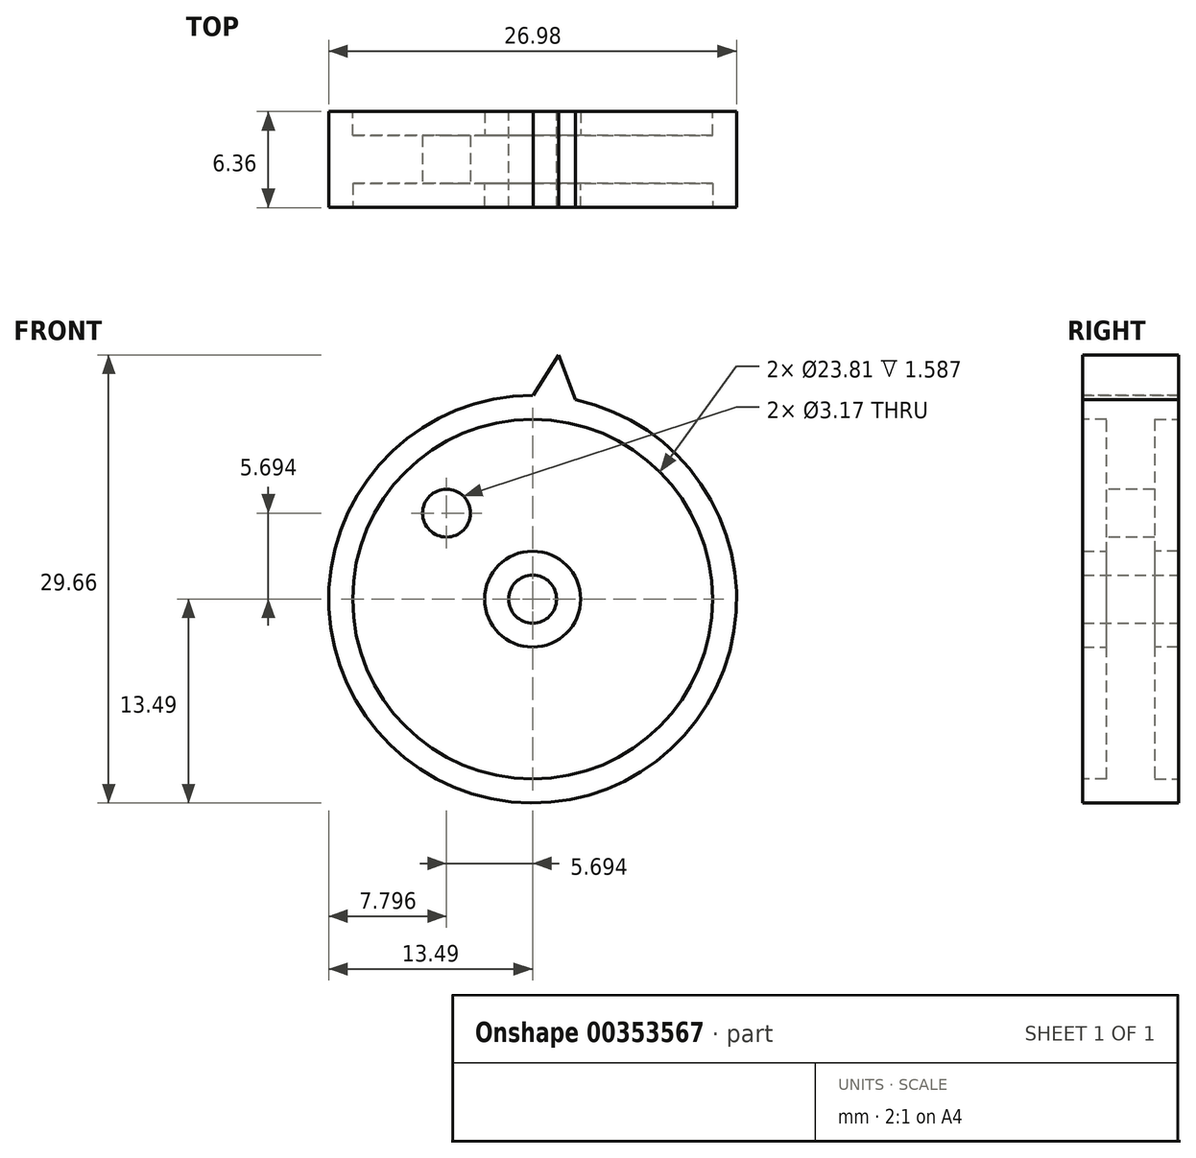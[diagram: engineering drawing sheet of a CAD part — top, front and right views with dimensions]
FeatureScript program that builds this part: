
annotation { "Feature Type Name" : "Feature", "Feature Type Description" : "" }
export const myFeature = defineFeature(function(context is Context, id is Id, definition is map)
    precondition{}
    {
        {
            var Q0;
            Q0=qCreatedBy(makeId("Front.planeOp"),FACE);
            var sketch = newSketch(context, id + "F0", { "sketchPlane" : qUnion([Q0])});
            skCircle(sketch, "E0", {"center": v(0, 0) * mm, "radius": 13.5 * mm});
            skSolve(sketch);
        }
        {
            var Q0;
            Q0 = qSketchRegion(id + "F0", true);
            extrude(context, id + "F1", {"entities" : qUnion([Q0]), "depth" : 6.35 * mm, "symmetric" : true});
        }
        {
            var Q0;
            Q0=makeQuery(id+"F1.opExtrude","CAP_FACE",FACE,{"disambiguationData":[OSD([sQuery(id+"F0.wireOp",EDGE,"E0")])],"isStart":false});
            var sketch = newSketch(context, id + "F2", { "sketchPlane" : qUnion([Q0])});
            skLineSegment(sketch, "E1", {"start": v(0.02, 13.5) * mm, "end": v(1.73, 16.17) * mm});
            skLineSegment(sketch, "E2", {"start": v(1.73, 16.17) * mm, "end": v(2.83, 13.2) * mm});
            skLineSegment(sketch, "E3", {"start": v(0, 0) * mm, "end": v(0.02, 13.5) * mm, "construction": true});
            skLineSegment(sketch, "E4", {"start": v(0, 0) * mm, "end": v(2.83, 13.2) * mm, "construction": true});
            skArc(sketch, "E5.0", {"start": v(2.83, 13.2) * mm, "mid": v(1.43, 13.42) * mm, "end": v(0.02, 13.5) * mm});
            skSolve(sketch);
        }
        {
            var Q0;
            Q0 = qSketchRegion(id + "F2", true);
            extrude(context, id + "F3", {"entities" : qUnion([Q0]), "operationType" : NewBodyOperationType.ADD, "oppositeDirection" : true, "depth" : 6.35 * mm});
        }
        {
            var Q0;
            {var subQ0=sQuery(id+"F2.wireOp",EDGE,"E5.0");var subQ1=sQuery(id+"F2.wireOp",EDGE,"E2");var subQ2=sQuery(id+"F2.wireOp",EDGE,"E1");Q0=makeQuery(id+"Fj7QE7v1GZ9bRCr_1.29.F3.boolean.opBoolean","MERGE",FACE,{"derivedFrom":[makeQuery(id+"Fj7QE7v1GZ9bRCr_1.28.F3.boolean.opBoolean","MERGE",FACE,{"derivedFrom":[makeQuery(id+"Fj7QE7v1GZ9bRCr_1.27.F3.boolean.opBoolean","MERGE",FACE,{"derivedFrom":[makeQuery(id+"Fj7QE7v1GZ9bRCr_1.26.F3.boolean.opBoolean","MERGE",FACE,{"derivedFrom":[makeQuery(id+"Fj7QE7v1GZ9bRCr_1.25.F3.boolean.opBoolean","MERGE",FACE,{"derivedFrom":[makeQuery(id+"Fj7QE7v1GZ9bRCr_1.24.F3.boolean.opBoolean","MERGE",FACE,{"derivedFrom":[makeQuery(id+"Fj7QE7v1GZ9bRCr_1.23.F3.boolean.opBoolean","MERGE",FACE,{"derivedFrom":[makeQuery(id+"Fj7QE7v1GZ9bRCr_1.22.F3.boolean.opBoolean","MERGE",FACE,{"derivedFrom":[makeQuery(id+"Fj7QE7v1GZ9bRCr_1.21.F3.boolean.opBoolean","MERGE",FACE,{"derivedFrom":[makeQuery(id+"Fj7QE7v1GZ9bRCr_1.20.F3.boolean.opBoolean","MERGE",FACE,{"derivedFrom":[makeQuery(id+"Fj7QE7v1GZ9bRCr_1.19.F3.boolean.opBoolean","MERGE",FACE,{"derivedFrom":[makeQuery(id+"Fj7QE7v1GZ9bRCr_1.18.F3.boolean.opBoolean","MERGE",FACE,{"derivedFrom":[makeQuery(id+"Fj7QE7v1GZ9bRCr_1.17.F3.boolean.opBoolean","MERGE",FACE,{"derivedFrom":[makeQuery(id+"Fj7QE7v1GZ9bRCr_1.16.F3.boolean.opBoolean","MERGE",FACE,{"derivedFrom":[makeQuery(id+"Fj7QE7v1GZ9bRCr_1.15.F3.boolean.opBoolean","MERGE",FACE,{"derivedFrom":[makeQuery(id+"Fj7QE7v1GZ9bRCr_1.14.F3.boolean.opBoolean","MERGE",FACE,{"derivedFrom":[makeQuery(id+"Fj7QE7v1GZ9bRCr_1.13.F3.boolean.opBoolean","MERGE",FACE,{"derivedFrom":[makeQuery(id+"Fj7QE7v1GZ9bRCr_1.12.F3.boolean.opBoolean","MERGE",FACE,{"derivedFrom":[makeQuery(id+"Fj7QE7v1GZ9bRCr_1.11.F3.boolean.opBoolean","MERGE",FACE,{"derivedFrom":[makeQuery(id+"Fj7QE7v1GZ9bRCr_1.10.F3.boolean.opBoolean","MERGE",FACE,{"derivedFrom":[makeQuery(id+"Fj7QE7v1GZ9bRCr_1.9.F3.boolean.opBoolean","MERGE",FACE,{"derivedFrom":[makeQuery(id+"Fj7QE7v1GZ9bRCr_1.8.F3.boolean.opBoolean","MERGE",FACE,{"derivedFrom":[makeQuery(id+"Fj7QE7v1GZ9bRCr_1.7.F3.boolean.opBoolean","MERGE",FACE,{"derivedFrom":[makeQuery(id+"Fj7QE7v1GZ9bRCr_1.6.F3.boolean.opBoolean","MERGE",FACE,{"derivedFrom":[makeQuery(id+"Fj7QE7v1GZ9bRCr_1.5.F3.boolean.opBoolean","MERGE",FACE,{"derivedFrom":[makeQuery(id+"Fj7QE7v1GZ9bRCr_1.4.F3.boolean.opBoolean","MERGE",FACE,{"derivedFrom":[makeQuery(id+"Fj7QE7v1GZ9bRCr_1.3.F3.boolean.opBoolean","MERGE",FACE,{"derivedFrom":[makeQuery(id+"Fj7QE7v1GZ9bRCr_1.2.F3.boolean.opBoolean","MERGE",FACE,{"derivedFrom":[makeQuery(id+"Fj7QE7v1GZ9bRCr_1.1.F3.boolean.opBoolean","MERGE",FACE,{"derivedFrom":[makeQuery(id+"F3.boolean.opBoolean","MERGE",FACE,{"derivedFrom":[makeQuery(id+"F1.opExtrude","CAP_FACE",FACE,{"disambiguationData":[OSD([sQuery(id+"F0.wireOp",EDGE,"E0")])],"isStart":false}),makeQuery(id+"F3.opExtrude","CAP_FACE",FACE,{"disambiguationData":[OSD([subQ2,subQ1,subQ0])],"isStart":true})]}),makeQuery(id+"Fj7QE7v1GZ9bRCr_1.1.F3.opExtrude","CAP_FACE",FACE,{"disambiguationData":[OSD([subQ2,subQ1,subQ0])],"isStart":true})]}),makeQuery(id+"Fj7QE7v1GZ9bRCr_1.2.F3.opExtrude","CAP_FACE",FACE,{"disambiguationData":[OSD([subQ2,subQ1,subQ0])],"isStart":true})]}),makeQuery(id+"Fj7QE7v1GZ9bRCr_1.3.F3.opExtrude","CAP_FACE",FACE,{"disambiguationData":[OSD([subQ2,subQ1,subQ0])],"isStart":true})]}),makeQuery(id+"Fj7QE7v1GZ9bRCr_1.4.F3.opExtrude","CAP_FACE",FACE,{"disambiguationData":[OSD([subQ2,subQ1,subQ0])],"isStart":true})]}),makeQuery(id+"Fj7QE7v1GZ9bRCr_1.5.F3.opExtrude","CAP_FACE",FACE,{"disambiguationData":[OSD([subQ2,subQ1,subQ0])],"isStart":true})]}),makeQuery(id+"Fj7QE7v1GZ9bRCr_1.6.F3.opExtrude","CAP_FACE",FACE,{"disambiguationData":[OSD([subQ2,subQ1,subQ0])],"isStart":true})]}),makeQuery(id+"Fj7QE7v1GZ9bRCr_1.7.F3.opExtrude","CAP_FACE",FACE,{"disambiguationData":[OSD([subQ2,subQ1,subQ0])],"isStart":true})]}),makeQuery(id+"Fj7QE7v1GZ9bRCr_1.8.F3.opExtrude","CAP_FACE",FACE,{"disambiguationData":[OSD([subQ2,subQ1,subQ0])],"isStart":true})]}),makeQuery(id+"Fj7QE7v1GZ9bRCr_1.9.F3.opExtrude","CAP_FACE",FACE,{"disambiguationData":[OSD([subQ2,subQ1,subQ0])],"isStart":true})]}),makeQuery(id+"Fj7QE7v1GZ9bRCr_1.10.F3.opExtrude","CAP_FACE",FACE,{"disambiguationData":[OSD([subQ2,subQ1,subQ0])],"isStart":true})]}),makeQuery(id+"Fj7QE7v1GZ9bRCr_1.11.F3.opExtrude","CAP_FACE",FACE,{"disambiguationData":[OSD([subQ2,subQ1,subQ0])],"isStart":true})]}),makeQuery(id+"Fj7QE7v1GZ9bRCr_1.12.F3.opExtrude","CAP_FACE",FACE,{"disambiguationData":[OSD([subQ2,subQ1,subQ0])],"isStart":true})]}),makeQuery(id+"Fj7QE7v1GZ9bRCr_1.13.F3.opExtrude","CAP_FACE",FACE,{"disambiguationData":[OSD([subQ2,subQ1,subQ0])],"isStart":true})]}),makeQuery(id+"Fj7QE7v1GZ9bRCr_1.14.F3.opExtrude","CAP_FACE",FACE,{"disambiguationData":[OSD([subQ2,subQ1,subQ0])],"isStart":true})]}),makeQuery(id+"Fj7QE7v1GZ9bRCr_1.15.F3.opExtrude","CAP_FACE",FACE,{"disambiguationData":[OSD([subQ2,subQ1,subQ0])],"isStart":true})]}),makeQuery(id+"Fj7QE7v1GZ9bRCr_1.16.F3.opExtrude","CAP_FACE",FACE,{"disambiguationData":[OSD([subQ2,subQ1,subQ0])],"isStart":true})]}),makeQuery(id+"Fj7QE7v1GZ9bRCr_1.17.F3.opExtrude","CAP_FACE",FACE,{"disambiguationData":[OSD([subQ2,subQ1,subQ0])],"isStart":true})]}),makeQuery(id+"Fj7QE7v1GZ9bRCr_1.18.F3.opExtrude","CAP_FACE",FACE,{"disambiguationData":[OSD([subQ2,subQ1,subQ0])],"isStart":true})]}),makeQuery(id+"Fj7QE7v1GZ9bRCr_1.19.F3.opExtrude","CAP_FACE",FACE,{"disambiguationData":[OSD([subQ2,subQ1,subQ0])],"isStart":true})]}),makeQuery(id+"Fj7QE7v1GZ9bRCr_1.20.F3.opExtrude","CAP_FACE",FACE,{"disambiguationData":[OSD([subQ2,subQ1,subQ0])],"isStart":true})]}),makeQuery(id+"Fj7QE7v1GZ9bRCr_1.21.F3.opExtrude","CAP_FACE",FACE,{"disambiguationData":[OSD([subQ2,subQ1,subQ0])],"isStart":true})]}),makeQuery(id+"Fj7QE7v1GZ9bRCr_1.22.F3.opExtrude","CAP_FACE",FACE,{"disambiguationData":[OSD([subQ2,subQ1,subQ0])],"isStart":true})]}),makeQuery(id+"Fj7QE7v1GZ9bRCr_1.23.F3.opExtrude","CAP_FACE",FACE,{"disambiguationData":[OSD([subQ2,subQ1,subQ0])],"isStart":true})]}),makeQuery(id+"Fj7QE7v1GZ9bRCr_1.24.F3.opExtrude","CAP_FACE",FACE,{"disambiguationData":[OSD([subQ2,subQ1,subQ0])],"isStart":true})]}),makeQuery(id+"Fj7QE7v1GZ9bRCr_1.25.F3.opExtrude","CAP_FACE",FACE,{"disambiguationData":[OSD([subQ2,subQ1,subQ0])],"isStart":true})]}),makeQuery(id+"Fj7QE7v1GZ9bRCr_1.26.F3.opExtrude","CAP_FACE",FACE,{"disambiguationData":[OSD([subQ2,subQ1,subQ0])],"isStart":true})]}),makeQuery(id+"Fj7QE7v1GZ9bRCr_1.27.F3.opExtrude","CAP_FACE",FACE,{"disambiguationData":[OSD([subQ2,subQ1,subQ0])],"isStart":true})]}),makeQuery(id+"Fj7QE7v1GZ9bRCr_1.28.F3.opExtrude","CAP_FACE",FACE,{"disambiguationData":[OSD([subQ2,subQ1,subQ0])],"isStart":true})]}),makeQuery(id+"Fj7QE7v1GZ9bRCr_1.29.F3.opExtrude","CAP_FACE",FACE,{"disambiguationData":[OSD([subQ2,subQ1,subQ0])],"isStart":true})]});}
            var sketch = newSketch(context, id + "F4", { "sketchPlane" : qUnion([Q0])});
            skCircle(sketch, "E6", {"center": v(0, 0) * mm, "radius": 11.9 * mm});
            skSolve(sketch);
        }
        {
            var Q0;
            Q0 = qSketchRegion(id + "F4", true);
            extrude(context, id + "F5", {"entities" : qUnion([Q0]), "operationType" : NewBodyOperationType.REMOVE, "oppositeDirection" : true, "depth" : 1.59 * mm});
        }
        {
            var Q0;
            {var subQ0=sQuery(id+"F2.wireOp",EDGE,"E5.0");var subQ1=sQuery(id+"F2.wireOp",EDGE,"E2");var subQ2=sQuery(id+"F2.wireOp",EDGE,"E1");Q0=makeQuery(id+"Fj7QE7v1GZ9bRCr_1.29.F3.boolean.opBoolean","MERGE",FACE,{"derivedFrom":[makeQuery(id+"Fj7QE7v1GZ9bRCr_1.28.F3.boolean.opBoolean","MERGE",FACE,{"derivedFrom":[makeQuery(id+"Fj7QE7v1GZ9bRCr_1.27.F3.boolean.opBoolean","MERGE",FACE,{"derivedFrom":[makeQuery(id+"Fj7QE7v1GZ9bRCr_1.26.F3.boolean.opBoolean","MERGE",FACE,{"derivedFrom":[makeQuery(id+"Fj7QE7v1GZ9bRCr_1.25.F3.boolean.opBoolean","MERGE",FACE,{"derivedFrom":[makeQuery(id+"Fj7QE7v1GZ9bRCr_1.24.F3.boolean.opBoolean","MERGE",FACE,{"derivedFrom":[makeQuery(id+"Fj7QE7v1GZ9bRCr_1.23.F3.boolean.opBoolean","MERGE",FACE,{"derivedFrom":[makeQuery(id+"Fj7QE7v1GZ9bRCr_1.22.F3.boolean.opBoolean","MERGE",FACE,{"derivedFrom":[makeQuery(id+"Fj7QE7v1GZ9bRCr_1.21.F3.boolean.opBoolean","MERGE",FACE,{"derivedFrom":[makeQuery(id+"Fj7QE7v1GZ9bRCr_1.20.F3.boolean.opBoolean","MERGE",FACE,{"derivedFrom":[makeQuery(id+"Fj7QE7v1GZ9bRCr_1.19.F3.boolean.opBoolean","MERGE",FACE,{"derivedFrom":[makeQuery(id+"Fj7QE7v1GZ9bRCr_1.18.F3.boolean.opBoolean","MERGE",FACE,{"derivedFrom":[makeQuery(id+"Fj7QE7v1GZ9bRCr_1.17.F3.boolean.opBoolean","MERGE",FACE,{"derivedFrom":[makeQuery(id+"Fj7QE7v1GZ9bRCr_1.16.F3.boolean.opBoolean","MERGE",FACE,{"derivedFrom":[makeQuery(id+"Fj7QE7v1GZ9bRCr_1.15.F3.boolean.opBoolean","MERGE",FACE,{"derivedFrom":[makeQuery(id+"Fj7QE7v1GZ9bRCr_1.14.F3.boolean.opBoolean","MERGE",FACE,{"derivedFrom":[makeQuery(id+"Fj7QE7v1GZ9bRCr_1.13.F3.boolean.opBoolean","MERGE",FACE,{"derivedFrom":[makeQuery(id+"Fj7QE7v1GZ9bRCr_1.12.F3.boolean.opBoolean","MERGE",FACE,{"derivedFrom":[makeQuery(id+"Fj7QE7v1GZ9bRCr_1.11.F3.boolean.opBoolean","MERGE",FACE,{"derivedFrom":[makeQuery(id+"Fj7QE7v1GZ9bRCr_1.10.F3.boolean.opBoolean","MERGE",FACE,{"derivedFrom":[makeQuery(id+"Fj7QE7v1GZ9bRCr_1.9.F3.boolean.opBoolean","MERGE",FACE,{"derivedFrom":[makeQuery(id+"Fj7QE7v1GZ9bRCr_1.8.F3.boolean.opBoolean","MERGE",FACE,{"derivedFrom":[makeQuery(id+"Fj7QE7v1GZ9bRCr_1.7.F3.boolean.opBoolean","MERGE",FACE,{"derivedFrom":[makeQuery(id+"Fj7QE7v1GZ9bRCr_1.6.F3.boolean.opBoolean","MERGE",FACE,{"derivedFrom":[makeQuery(id+"Fj7QE7v1GZ9bRCr_1.5.F3.boolean.opBoolean","MERGE",FACE,{"derivedFrom":[makeQuery(id+"Fj7QE7v1GZ9bRCr_1.4.F3.boolean.opBoolean","MERGE",FACE,{"derivedFrom":[makeQuery(id+"Fj7QE7v1GZ9bRCr_1.3.F3.boolean.opBoolean","MERGE",FACE,{"derivedFrom":[makeQuery(id+"Fj7QE7v1GZ9bRCr_1.2.F3.boolean.opBoolean","MERGE",FACE,{"derivedFrom":[makeQuery(id+"Fj7QE7v1GZ9bRCr_1.1.F3.boolean.opBoolean","MERGE",FACE,{"derivedFrom":[makeQuery(id+"F3.boolean.opBoolean","MERGE",FACE,{"derivedFrom":[makeQuery(id+"F1.opExtrude","CAP_FACE",FACE,{"disambiguationData":[OSD([sQuery(id+"F0.wireOp",EDGE,"E0")])],"isStart":true}),makeQuery(id+"F3.opExtrude","CAP_FACE",FACE,{"disambiguationData":[OSD([subQ2,subQ1,subQ0])],"isStart":false})]}),makeQuery(id+"Fj7QE7v1GZ9bRCr_1.1.F3.opExtrude","CAP_FACE",FACE,{"disambiguationData":[OSD([subQ2,subQ1,subQ0])],"isStart":false})]}),makeQuery(id+"Fj7QE7v1GZ9bRCr_1.2.F3.opExtrude","CAP_FACE",FACE,{"disambiguationData":[OSD([subQ2,subQ1,subQ0])],"isStart":false})]}),makeQuery(id+"Fj7QE7v1GZ9bRCr_1.3.F3.opExtrude","CAP_FACE",FACE,{"disambiguationData":[OSD([subQ2,subQ1,subQ0])],"isStart":false})]}),makeQuery(id+"Fj7QE7v1GZ9bRCr_1.4.F3.opExtrude","CAP_FACE",FACE,{"disambiguationData":[OSD([subQ2,subQ1,subQ0])],"isStart":false})]}),makeQuery(id+"Fj7QE7v1GZ9bRCr_1.5.F3.opExtrude","CAP_FACE",FACE,{"disambiguationData":[OSD([subQ2,subQ1,subQ0])],"isStart":false})]}),makeQuery(id+"Fj7QE7v1GZ9bRCr_1.6.F3.opExtrude","CAP_FACE",FACE,{"disambiguationData":[OSD([subQ2,subQ1,subQ0])],"isStart":false})]}),makeQuery(id+"Fj7QE7v1GZ9bRCr_1.7.F3.opExtrude","CAP_FACE",FACE,{"disambiguationData":[OSD([subQ2,subQ1,subQ0])],"isStart":false})]}),makeQuery(id+"Fj7QE7v1GZ9bRCr_1.8.F3.opExtrude","CAP_FACE",FACE,{"disambiguationData":[OSD([subQ2,subQ1,subQ0])],"isStart":false})]}),makeQuery(id+"Fj7QE7v1GZ9bRCr_1.9.F3.opExtrude","CAP_FACE",FACE,{"disambiguationData":[OSD([subQ2,subQ1,subQ0])],"isStart":false})]}),makeQuery(id+"Fj7QE7v1GZ9bRCr_1.10.F3.opExtrude","CAP_FACE",FACE,{"disambiguationData":[OSD([subQ2,subQ1,subQ0])],"isStart":false})]}),makeQuery(id+"Fj7QE7v1GZ9bRCr_1.11.F3.opExtrude","CAP_FACE",FACE,{"disambiguationData":[OSD([subQ2,subQ1,subQ0])],"isStart":false})]}),makeQuery(id+"Fj7QE7v1GZ9bRCr_1.12.F3.opExtrude","CAP_FACE",FACE,{"disambiguationData":[OSD([subQ2,subQ1,subQ0])],"isStart":false})]}),makeQuery(id+"Fj7QE7v1GZ9bRCr_1.13.F3.opExtrude","CAP_FACE",FACE,{"disambiguationData":[OSD([subQ2,subQ1,subQ0])],"isStart":false})]}),makeQuery(id+"Fj7QE7v1GZ9bRCr_1.14.F3.opExtrude","CAP_FACE",FACE,{"disambiguationData":[OSD([subQ2,subQ1,subQ0])],"isStart":false})]}),makeQuery(id+"Fj7QE7v1GZ9bRCr_1.15.F3.opExtrude","CAP_FACE",FACE,{"disambiguationData":[OSD([subQ2,subQ1,subQ0])],"isStart":false})]}),makeQuery(id+"Fj7QE7v1GZ9bRCr_1.16.F3.opExtrude","CAP_FACE",FACE,{"disambiguationData":[OSD([subQ2,subQ1,subQ0])],"isStart":false})]}),makeQuery(id+"Fj7QE7v1GZ9bRCr_1.17.F3.opExtrude","CAP_FACE",FACE,{"disambiguationData":[OSD([subQ2,subQ1,subQ0])],"isStart":false})]}),makeQuery(id+"Fj7QE7v1GZ9bRCr_1.18.F3.opExtrude","CAP_FACE",FACE,{"disambiguationData":[OSD([subQ2,subQ1,subQ0])],"isStart":false})]}),makeQuery(id+"Fj7QE7v1GZ9bRCr_1.19.F3.opExtrude","CAP_FACE",FACE,{"disambiguationData":[OSD([subQ2,subQ1,subQ0])],"isStart":false})]}),makeQuery(id+"Fj7QE7v1GZ9bRCr_1.20.F3.opExtrude","CAP_FACE",FACE,{"disambiguationData":[OSD([subQ2,subQ1,subQ0])],"isStart":false})]}),makeQuery(id+"Fj7QE7v1GZ9bRCr_1.21.F3.opExtrude","CAP_FACE",FACE,{"disambiguationData":[OSD([subQ2,subQ1,subQ0])],"isStart":false})]}),makeQuery(id+"Fj7QE7v1GZ9bRCr_1.22.F3.opExtrude","CAP_FACE",FACE,{"disambiguationData":[OSD([subQ2,subQ1,subQ0])],"isStart":false})]}),makeQuery(id+"Fj7QE7v1GZ9bRCr_1.23.F3.opExtrude","CAP_FACE",FACE,{"disambiguationData":[OSD([subQ2,subQ1,subQ0])],"isStart":false})]}),makeQuery(id+"Fj7QE7v1GZ9bRCr_1.24.F3.opExtrude","CAP_FACE",FACE,{"disambiguationData":[OSD([subQ2,subQ1,subQ0])],"isStart":false})]}),makeQuery(id+"Fj7QE7v1GZ9bRCr_1.25.F3.opExtrude","CAP_FACE",FACE,{"disambiguationData":[OSD([subQ2,subQ1,subQ0])],"isStart":false})]}),makeQuery(id+"Fj7QE7v1GZ9bRCr_1.26.F3.opExtrude","CAP_FACE",FACE,{"disambiguationData":[OSD([subQ2,subQ1,subQ0])],"isStart":false})]}),makeQuery(id+"Fj7QE7v1GZ9bRCr_1.27.F3.opExtrude","CAP_FACE",FACE,{"disambiguationData":[OSD([subQ2,subQ1,subQ0])],"isStart":false})]}),makeQuery(id+"Fj7QE7v1GZ9bRCr_1.28.F3.opExtrude","CAP_FACE",FACE,{"disambiguationData":[OSD([subQ2,subQ1,subQ0])],"isStart":false})]}),makeQuery(id+"Fj7QE7v1GZ9bRCr_1.29.F3.opExtrude","CAP_FACE",FACE,{"disambiguationData":[OSD([subQ2,subQ1,subQ0])],"isStart":false})]});}
            var sketch = newSketch(context, id + "F6", { "sketchPlane" : qUnion([Q0])});
            skCircle(sketch, "E7.0", {"center": v(0, 0) * mm, "radius": 11.9 * mm});
            skSolve(sketch);
        }
        {
            var Q0;
            Q0 = qSketchRegion(id + "F6", true);
            extrude(context, id + "F7", {"entities" : qUnion([Q0]), "operationType" : NewBodyOperationType.REMOVE, "oppositeDirection" : true, "depth" : 1.59 * mm});
        }
        {
            var Q0;
            Q0=makeQuery(id+"F5.boolean.opBoolean","COPY",FACE,{"derivedFrom":makeQuery(id+"F5.opExtrude","CAP_FACE",FACE,{"disambiguationData":[OSD([sQuery(id+"F4.wireOp",EDGE,"E6")])],"isStart":false})});
            var sketch = newSketch(context, id + "F8", { "sketchPlane" : qUnion([Q0])});
            skCircle(sketch, "E8", {"center": v(-5.7, 5.7) * mm, "radius": 1.59 * mm});
            skLineSegment(sketch, "E9", {"start": v(-5.7, 5.7) * mm, "end": v(-5.7, 10.46) * mm, "construction": true});
            skLineSegment(sketch, "E10", {"start": v(-5.7, 10.46) * mm, "end": v(-10.46, 5.7) * mm, "construction": true});
            skLineSegment(sketch, "E11", {"start": v(-10.46, 5.7) * mm, "end": v(-5.7, 5.7) * mm, "construction": true});
            skSolve(sketch);
        }
        {
            var Q0;
            Q0 = qSketchRegion(id + "F8", true);
            extrude(context, id + "F9", {"entities" : qUnion([Q0]), "operationType" : NewBodyOperationType.REMOVE, "endBound" : BoundingType.THROUGH_ALL, "oppositeDirection" : true, "depth" : 25.4 * mm});
        }
        {
            var Q0;
            Q0=makeQuery(id+"F5.boolean.opBoolean","COPY",FACE,{"derivedFrom":makeQuery(id+"F5.opExtrude","CAP_FACE",FACE,{"disambiguationData":[OSD([sQuery(id+"F4.wireOp",EDGE,"E6")])],"isStart":false})});
            var sketch = newSketch(context, id + "F10", { "sketchPlane" : qUnion([Q0])});
            skCircle(sketch, "E12", {"center": v(0, 0) * mm, "radius": 3.18 * mm});
            skSolve(sketch);
        }
        {
            var Q0;
            Q0 = qSketchRegion(id + "F10", true);
            extrude(context, id + "F11", {"entities" : qUnion([Q0]), "operationType" : NewBodyOperationType.ADD, "depth" : 1.59 * mm});
        }
        {
            var Q0;
            Q0=makeQuery(id+"F7.boolean.opBoolean","COPY",FACE,{"derivedFrom":makeQuery(id+"F7.opExtrude","CAP_FACE",FACE,{"disambiguationData":[OSD([sQuery(id+"F6.wireOp",EDGE,"E7.0")])],"isStart":false})});
            var sketch = newSketch(context, id + "F12", { "sketchPlane" : qUnion([Q0])});
            skCircle(sketch, "E13", {"center": v(0, 0) * mm, "radius": 3.18 * mm});
            skSolve(sketch);
        }
        {
            var Q0;
            Q0 = qSketchRegion(id + "F12", true);
            extrude(context, id + "F13", {"entities" : qUnion([Q0]), "operationType" : NewBodyOperationType.ADD, "depth" : 1.59 * mm});
        }
        {
            var Q0;
            Q0=makeQuery(id+"F13.opExtrude","CAP_FACE",FACE,{"disambiguationData":[OSD([sQuery(id+"F12.wireOp",EDGE,"E13")])],"isStart":false});
            var sketch = newSketch(context, id + "F14", { "sketchPlane" : qUnion([Q0])});
            skCircle(sketch, "E14", {"center": v(0, 0) * mm, "radius": 1.59 * mm});
            skSolve(sketch);
        }
        {
            var Q0;
            Q0 = qSketchRegion(id + "F14", true);
            extrude(context, id + "F15", {"entities" : qUnion([Q0]), "operationType" : NewBodyOperationType.REMOVE, "endBound" : BoundingType.THROUGH_ALL, "oppositeDirection" : true, "depth" : 25.4 * mm});
        }
    });
